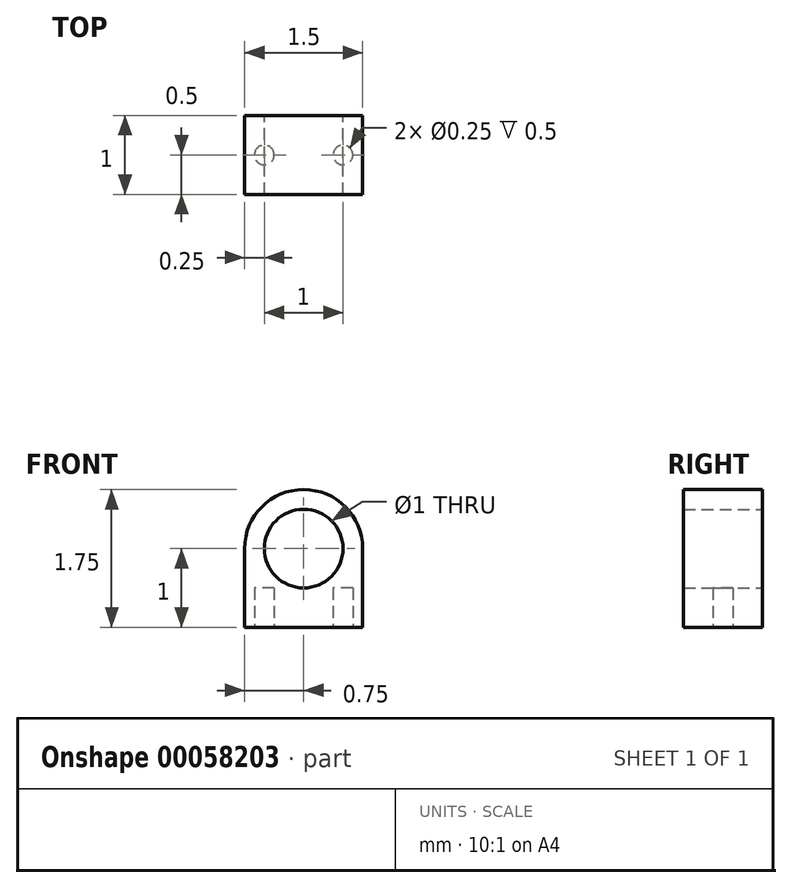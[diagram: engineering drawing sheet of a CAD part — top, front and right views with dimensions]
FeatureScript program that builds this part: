
annotation { "Feature Type Name" : "Feature", "Feature Type Description" : "" }
export const myFeature = defineFeature(function(context is Context, id is Id, definition is map)
    precondition{}
    {
        {
            var Q0;
            Q0=qCreatedBy(makeId("Front.planeOp"),FACE);
            var sketch = newSketch(context, id + "F0", { "sketchPlane" : qUnion([Q0])});
            skLineSegment(sketch, "E0", {"start": v(0, 0) * mm, "end": v(-0.75, 0) * mm});
            skLineSegment(sketch, "E1", {"start": v(-0.75, 0) * mm, "end": v(-0.75, 1) * mm});
            skArc(sketch, "E2", {"start": v(-0.75, 1) * mm, "mid": v(-0.53, 1.53) * mm, "end": v(0, 1.75) * mm});
            skCircle(sketch, "E3", {"center": v(0, 1) * mm, "radius": 0.5 * mm});
            skLineSegment(sketch, "E4.MirrorCS", {"start": v(0.75, 0) * mm, "end": v(0.75, 1) * mm});
            skLineSegment(sketch, "E5.MirrorCS", {"start": v(0, 0) * mm, "end": v(0.75, 0) * mm});
            skArc(sketch, "E6.MirrorCS", {"start": v(0.75, 1) * mm, "mid": v(0.53, 1.53) * mm, "end": v(0, 1.75) * mm});
            skSolve(sketch);
        }
        {
            var Q0;
            Q0=qSketchRegion(id+"F0",true);
            var Q1;
            Q1=makeQuery(id+"F0.imprint","IMPRINT",FACE,{"disambiguationData":[TD([[makeQuery(id+"F0.imprint","IMPRINT",EDGE,{"derivedFrom":sQuery(id+"F0.wireOp",EDGE,"E0")}),-1.0]])]});
            extrude(context, id + "F1", {"entities" : qUnion([Q0, Q1]), "endBound" : BoundingType.SYMMETRIC, "depth" : 1 * mm});
        }
        {
            var Q0;
            Q0=qCreatedBy(makeId("Top.planeOp"),FACE);
            var sketch = newSketch(context, id + "F2", { "sketchPlane" : qUnion([Q0])});
            skCircle(sketch, "E7", {"center": v(-0.5, 0) * mm, "radius": 0.12 * mm});
            skCircle(sketch, "E8", {"center": v(0.5, 0) * mm, "radius": 0.12 * mm});
            skSolve(sketch);
        }
        {
            var Q0;
            Q0=qSketchRegion(id+"F2",true);
            extrude(context, id + "F3", {"entities" : qUnion([Q0]), "operationType" : NewBodyOperationType.REMOVE, "depth" : 0.5 * mm});
        }
    });
